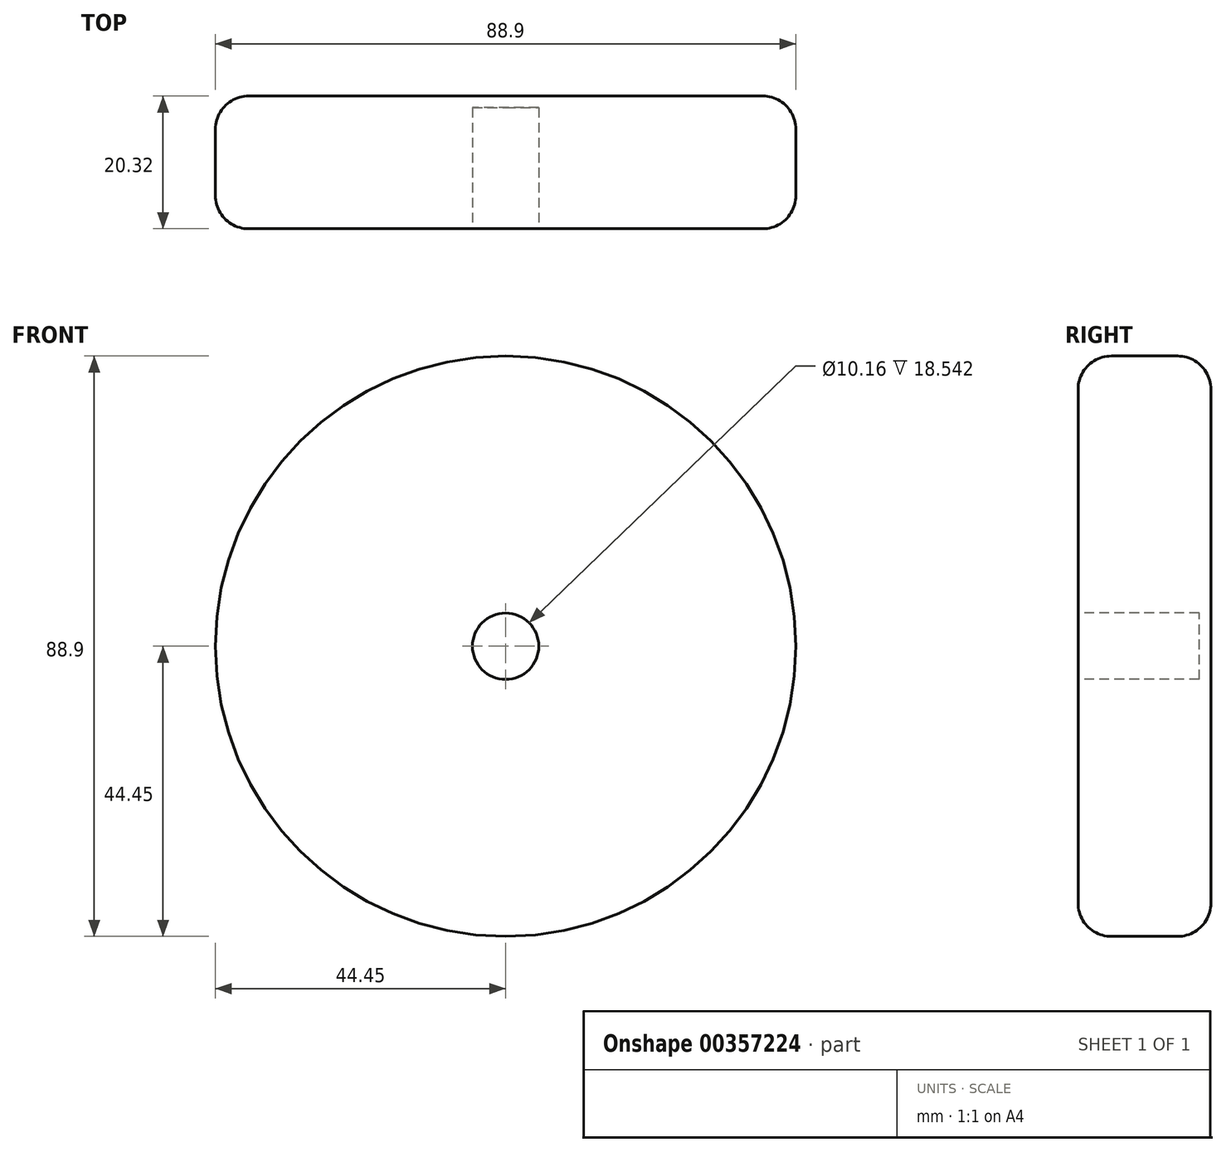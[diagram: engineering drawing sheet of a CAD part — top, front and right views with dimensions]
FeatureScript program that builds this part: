
annotation { "Feature Type Name" : "Feature", "Feature Type Description" : "" }
export const myFeature = defineFeature(function(context is Context, id is Id, definition is map)
    precondition{}
    {
        {
            var Q0;
            Q0=qCreatedBy(makeId("Front.planeOp"),FACE);
            var sketch = newSketch(context, id + "F0", { "sketchPlane" : qUnion([Q0])});
            skCircle(sketch, "E0", {"center": v(0, 0) * mm, "radius": 44.45 * mm});
            skSolve(sketch);
        }
        {
            var Q0;
            Q0=makeQuery(id+"F0.imprint","IMPRINT",FACE,{"disambiguationData":[TD([[makeQuery(id+"F0.imprint","IMPRINT",EDGE,{"derivedFrom":sQuery(id+"F0.wireOp",EDGE,"E0")}),1.0]])]});
            extrude(context, id + "F1", {"entities" : qUnion([Q0]), "depth" : 20.32 * mm});
        }
        {
            var Q0;
            Q0=makeQuery(id+"F1.opExtrude","CAP_FACE",FACE,{"disambiguationData":[OSD([sQuery(id+"F0.wireOp",EDGE,"E0")])],"isStart":false});
            var sketch = newSketch(context, id + "F2", { "sketchPlane" : qUnion([Q0])});
            skCircle(sketch, "E1", {"center": v(0, 0) * mm, "radius": 5.08 * mm});
            skSolve(sketch);
        }
        {
            var Q0;
            Q0=makeQuery(id+"F2.imprint","IMPRINT",FACE,{"disambiguationData":[TD([[makeQuery(id+"F2.imprint","IMPRINT",EDGE,{"derivedFrom":sQuery(id+"F2.wireOp",EDGE,"E1")}),1.0]])]});
            extrude(context, id + "F3", {"entities" : qUnion([Q0]), "operationType" : NewBodyOperationType.REMOVE, "oppositeDirection" : true, "depth" : 18.54 * mm});
        }
        {
            var Q0;
            Q0=makeQuery(id+"F1.opExtrude","CAP_EDGE",EDGE,{"disambiguationData":[OSD([sQuery(id+"F0.wireOp",EDGE,"E0")])],"isStart":false});
            var Q1;
            Q1=makeQuery(id+"F1.opExtrude","CAP_EDGE",EDGE,{"disambiguationData":[OSD([sQuery(id+"F0.wireOp",EDGE,"E0")])],"isStart":true});
            fillet(context, id + "F4", {"entities" : qUnion([Q0, Q1]), "radius" : 5.08 * mm, "tangentPropagation" : true, "allowEdgeOverflow" : false});
        }
    });
